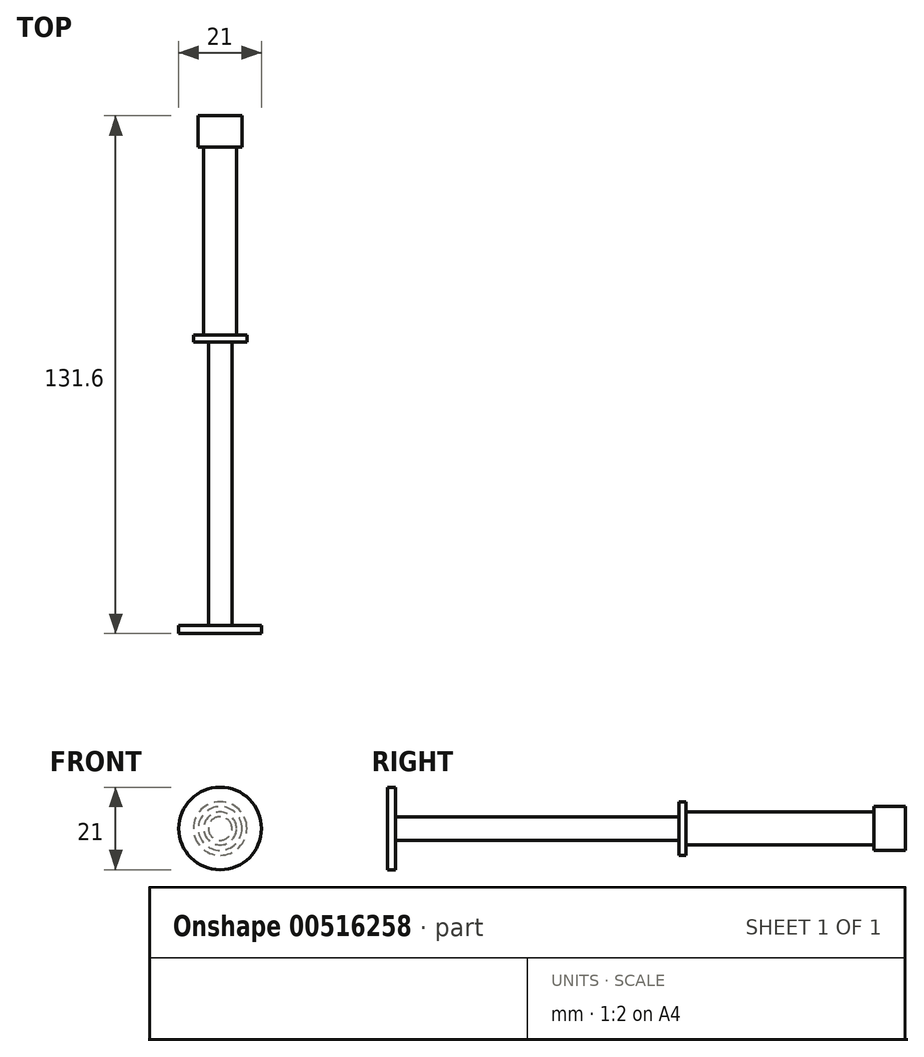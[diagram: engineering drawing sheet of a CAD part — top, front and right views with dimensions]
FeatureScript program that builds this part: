
annotation { "Feature Type Name" : "Feature", "Feature Type Description" : "" }
export const myFeature = defineFeature(function(context is Context, id is Id, definition is map)
    precondition{}
    {
        {
            var Q0;
            Q0=qCreatedBy(makeId("Front.planeOp"),FACE);
            var sketch = newSketch(context, id + "F0", { "sketchPlane" : qUnion([Q0])});
            skCircle(sketch, "E0", {"center": v(0, 0) * mm, "radius": 5.55 * mm});
            skSolve(sketch);
        }
        {
            var Q0;
            Q0 = qSketchRegion(id + "F0", true);
            extrude(context, id + "F1", {"entities" : qUnion([Q0]), "depth" : 8 * mm, "offsetDistance" : 25 * mm});
        }
        {
            var Q0;
            Q0=qCreatedBy(makeId("Front.planeOp"),FACE);
            var sketch = newSketch(context, id + "F2", { "sketchPlane" : qUnion([Q0])});
            skCircle(sketch, "E1", {"center": v(0, 0) * mm, "radius": 4.17 * mm});
            skSolve(sketch);
        }
        {
            var Q0;
            Q0 = qSketchRegion(id + "F2", true);
            extrude(context, id + "F3", {"entities" : qUnion([Q0]), "operationType" : NewBodyOperationType.ADD, "depth" : (63.7 - 8) * mm, "offsetDistance" : 25 * mm});
        }
        {
            var Q0;
            Q0=makeQuery(id+"F3.opExtrude","CAP_FACE",FACE,{"disambiguationData":[OSD([sQuery(id+"F2.wireOp",EDGE,"E1")])],"isStart":false});
            var sketch = newSketch(context, id + "F4", { "sketchPlane" : qUnion([Q0])});
            skCircle(sketch, "E2", {"center": v(0, 0) * mm, "radius": 6.8 * mm});
            skSolve(sketch);
        }
        {
            var Q0;
            Q0 = qSketchRegion(id + "F4", true);
            extrude(context, id + "F5", {"entities" : qUnion([Q0]), "operationType" : NewBodyOperationType.ADD, "depth" : 1.8 * mm, "offsetDistance" : 25 * mm});
        }
        {
            var Q0;
            Q0=makeQuery(id+"F5.opExtrude","CAP_FACE",FACE,{"disambiguationData":[OSD([sQuery(id+"F4.wireOp",EDGE,"E2")])],"isStart":false});
            var sketch = newSketch(context, id + "F6", { "sketchPlane" : qUnion([Q0])});
            skCircle(sketch, "E3", {"center": v(0, 0) * mm, "radius": 3 * mm});
            skSolve(sketch);
        }
        {
            var Q0;
            Q0 = qSketchRegion(id + "F6", true);
            extrude(context, id + "F7", {"entities" : qUnion([Q0]), "operationType" : NewBodyOperationType.ADD, "depth" : 72 * mm, "offsetDistance" : 25 * mm});
        }
        {
            var Q0;
            Q0=makeQuery(id+"F7.opExtrude","CAP_FACE",FACE,{"disambiguationData":[OSD([sQuery(id+"F6.wireOp",EDGE,"E3")])],"isStart":false});
            var sketch = newSketch(context, id + "F8", { "sketchPlane" : qUnion([Q0])});
            skCircle(sketch, "E4", {"center": v(0, 0) * mm, "radius": 10.5 * mm});
            skSolve(sketch);
        }
        {
            var Q0;
            Q0 = qSketchRegion(id + "F8", true);
            extrude(context, id + "F9", {"entities" : qUnion([Q0]), "operationType" : NewBodyOperationType.ADD, "depth" : 2.1 * mm, "offsetDistance" : 25 * mm});
        }
    });
